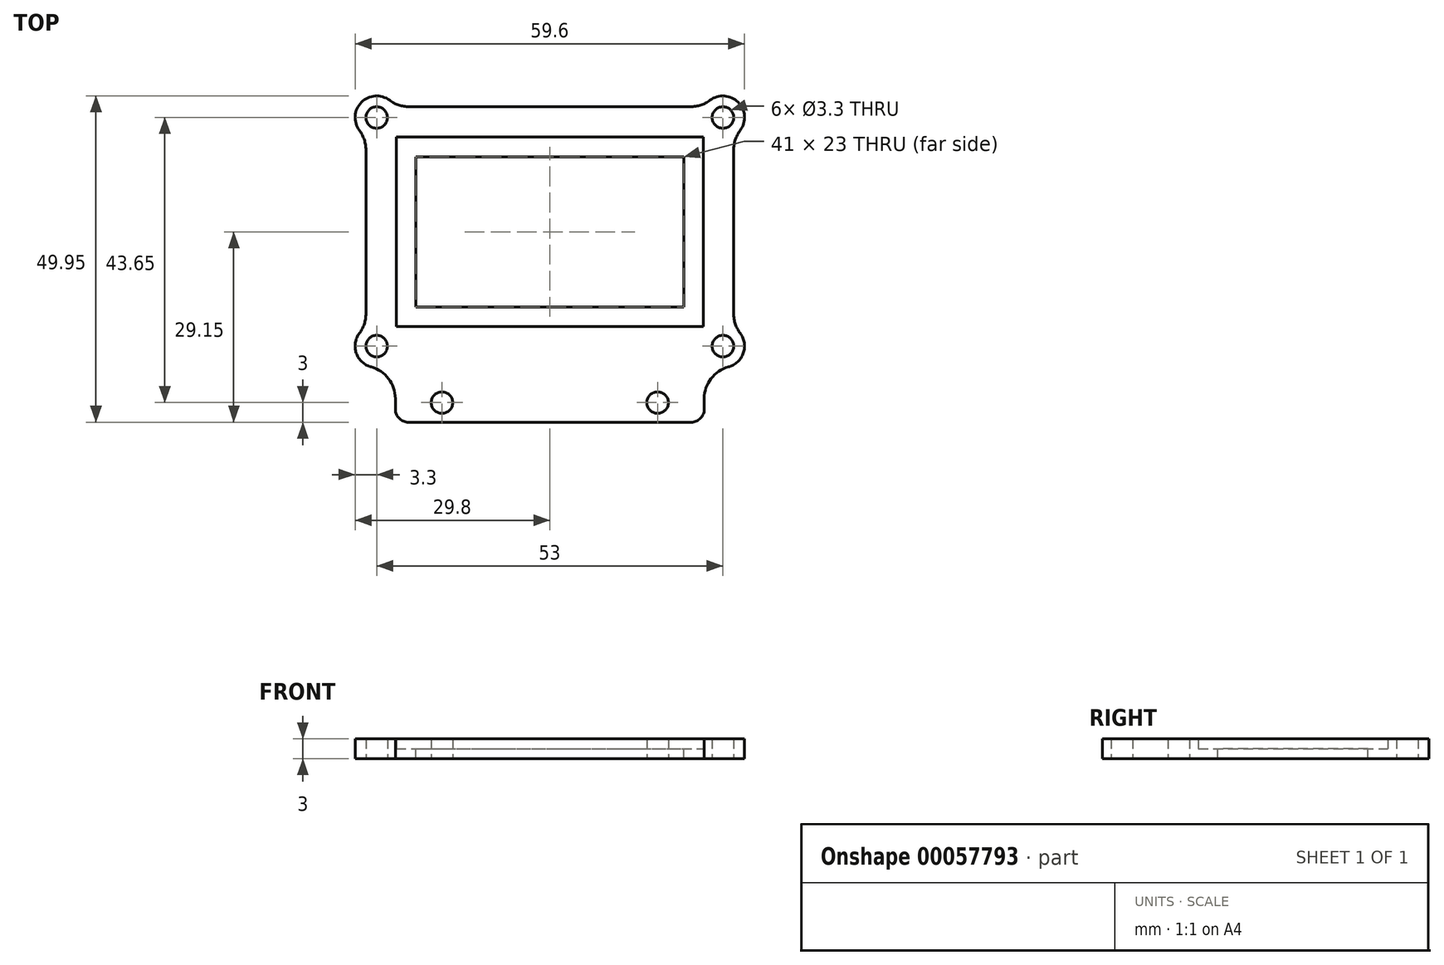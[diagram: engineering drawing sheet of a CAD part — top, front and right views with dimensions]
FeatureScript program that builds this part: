
annotation { "Feature Type Name" : "Feature", "Feature Type Description" : "" }
export const myFeature = defineFeature(function(context is Context, id is Id, definition is map)
    precondition{}
    {
        {
            var Q0;
            Q0=qCreatedBy(makeId("Top.planeOp"),FACE);
            var sketch = newSketch(context, id + "F0", { "sketchPlane" : qUnion([Q0])});
            skLineSegment(sketch, "E0", {"start": v(0, 0) * mm, "end": v(0, 49.8) * mm, "construction": true});
            skLineSegment(sketch, "E1.0", {"start": v(23.5, 0) * mm, "end": v(23.5, 29) * mm});
            skLineSegment(sketch, "E2.0", {"start": v(-23.5, 0) * mm, "end": v(-23.5, 29) * mm});
            skLineSegment(sketch, "E3", {"start": v(-23.5, 0) * mm, "end": v(23.5, 0) * mm});
            skLineSegment(sketch, "E4.0", {"start": v(-23.5, 29) * mm, "end": v(23.5, 29) * mm});
            skLineSegment(sketch, "E5.0", {"start": v(-26.5, 0) * mm, "end": v(-26.5, 33.65) * mm, "construction": true});
            skLineSegment(sketch, "E6.0", {"start": v(-26.5, 32) * mm, "end": v(30.75, 32) * mm, "construction": true});
            skLineSegment(sketch, "E7.0", {"start": v(26.5, 0) * mm, "end": v(26.5, 32) * mm, "construction": true});
            skLineSegment(sketch, "E8.0", {"start": v(-23.5, -3) * mm, "end": v(23.5, -3) * mm, "construction": true});
            skCircle(sketch, "E9", {"center": v(-26.5, 32) * mm, "radius": 1.65 * mm});
            skArc(sketch, "E10", {"start": v(-24.53, 34.64) * mm, "mid": v(-28.83, 34.33) * mm, "end": v(-29.14, 30.02) * mm});
            skArc(sketch, "E11.MirrorC", {"start": v(24.53, 34.64) * mm, "mid": v(28.83, 34.33) * mm, "end": v(29.14, 30.02) * mm});
            skCircle(sketch, "E12.MirrorC", {"center": v(26.5, 32) * mm, "radius": 1.65 * mm});
            skLineSegment(sketch, "E13", {"start": v(-21.53, 33.65) * mm, "end": v(21.53, 33.65) * mm});
            skLineSegment(sketch, "E14", {"start": v(-23.5, 14.5) * mm, "end": v(23.5, 14.5) * mm, "construction": true});
            skArc(sketch, "E15.MirrorC", {"start": v(-27.35, -6.19) * mm, "mid": v(-29.62, -4.08) * mm, "end": v(-29.14, -1.02) * mm});
            skCircle(sketch, "E16.MirrorC", {"center": v(-26.5, -3) * mm, "radius": 1.65 * mm});
            skArc(sketch, "E17.MirrorC", {"start": v(27.35, -6.19) * mm, "mid": v(29.62, -4.08) * mm, "end": v(29.14, -1.02) * mm});
            skCircle(sketch, "E18.MirrorC", {"center": v(26.5, -3) * mm, "radius": 1.65 * mm});
            skLineSegment(sketch, "E19", {"start": v(-28.15, 32.12) * mm, "end": v(-28.15, 31.88) * mm});
            skLineSegment(sketch, "E20.MirrorCS", {"start": v(28.15, 32.12) * mm, "end": v(28.15, 31.88) * mm});
            skLineSegment(sketch, "E21.trimOffspring", {"start": v(-28.15, 27.03) * mm, "end": v(-28.15, 1.97) * mm});
            skPoint(sketch, "E22.orphan", {"position": v(-28.15, -2.88) * mm});
            skPoint(sketch, "E23.orphan", {"position": v(28.15, -2.88) * mm});
            skLineSegment(sketch, "E24.trimOffspring", {"start": v(28.15, 27.03) * mm, "end": v(28.15, 1.97) * mm});
            skPoint(sketch, "E25.visualSharp", {"position": v(-28.15, 29.14) * mm});
            skArc(sketch, "E25.filletArc", {"start": v(-28.15, 27.03) * mm, "mid": v(-28.4, 28.6) * mm, "end": v(-29.14, 30.02) * mm});
            skPoint(sketch, "E26.visualSharp", {"position": v(-28.15, -0.14) * mm});
            skArc(sketch, "E26.filletArc", {"start": v(-29.14, -1.02) * mm, "mid": v(-28.4, 0.4) * mm, "end": v(-28.15, 1.97) * mm});
            skPoint(sketch, "E27.visualSharp", {"position": v(-23.64, 33.65) * mm});
            skArc(sketch, "E27.filletArc", {"start": v(-24.53, 34.64) * mm, "mid": v(-23.1, 33.9) * mm, "end": v(-21.53, 33.65) * mm});
            skPoint(sketch, "E28.visualSharp", {"position": v(23.64, 33.65) * mm});
            skArc(sketch, "E28.filletArc", {"start": v(21.53, 33.65) * mm, "mid": v(23.1, 33.9) * mm, "end": v(24.53, 34.64) * mm});
            skPoint(sketch, "E29.visualSharp", {"position": v(28.15, 29.14) * mm});
            skArc(sketch, "E29.filletArc", {"start": v(29.14, 30.02) * mm, "mid": v(28.4, 28.6) * mm, "end": v(28.15, 27.03) * mm});
            skPoint(sketch, "E30.visualSharp", {"position": v(28.15, -0.14) * mm});
            skArc(sketch, "E30.filletArc", {"start": v(28.15, 1.97) * mm, "mid": v(28.4, 0.4) * mm, "end": v(29.14, -1.02) * mm});
            skLineSegment(sketch, "E31", {"start": v(-23.64, -9.65) * mm, "end": v(-23.64, -9.65) * mm});
            skLineSegment(sketch, "E32", {"start": v(0, 0) * mm, "end": v(0, -14.65) * mm, "construction": true});
            skPoint(sketch, "E33.orphan", {"position": v(0, -6) * mm});
            skLineSegment(sketch, "E34.0", {"start": v(-16.5, 0) * mm, "end": v(-16.5, -14.65) * mm, "construction": true});
            skLineSegment(sketch, "E35.0", {"start": v(16.5, 0) * mm, "end": v(16.5, -14.65) * mm, "construction": true});
            skLineSegment(sketch, "E36.0", {"start": v(-23.64, -11.65) * mm, "end": v(23.64, -11.65) * mm, "construction": true});
            skCircle(sketch, "E37", {"center": v(-16.5, -11.65) * mm, "radius": 1.65 * mm});
            skCircle(sketch, "E38.MirrorC", {"center": v(16.5, -11.65) * mm, "radius": 1.65 * mm});
            skPoint(sketch, "E39.visualSharp", {"position": v(-23.64, -4.65) * mm});
            skArc(sketch, "E39.filletArc", {"start": v(-23.64, -11.02) * mm, "mid": v(-24.68, -7.97) * mm, "end": v(-27.35, -6.19) * mm});
            skPoint(sketch, "E40.visualSharp", {"position": v(-23.64, -14.65) * mm});
            skPoint(sketch, "E41.visualSharp", {"position": v(23.64, -4.65) * mm});
            skLineSegment(sketch, "E42", {"start": v(-21.64, -14.65) * mm, "end": v(21.64, -14.65) * mm});
            skLineSegment(sketch, "E43", {"start": v(23.64, -11.02) * mm, "end": v(23.64, -12.65) * mm});
            skArc(sketch, "E44.filletArc", {"start": v(27.35, -6.19) * mm, "mid": v(24.68, -7.97) * mm, "end": v(23.64, -11.02) * mm});
            skArc(sketch, "E45.filletArc", {"start": v(21.64, -14.65) * mm, "mid": v(23.06, -14.06) * mm, "end": v(23.64, -12.65) * mm});
            skLineSegment(sketch, "E46", {"start": v(-23.64, -11.02) * mm, "end": v(-23.64, -12.65) * mm});
            skArc(sketch, "E47.filletArc", {"start": v(-23.64, -12.65) * mm, "mid": v(-23.06, -14.06) * mm, "end": v(-21.64, -14.65) * mm});
            skSolve(sketch);
        }
        {
            var Q0;
            Q0=makeQuery(id+"F0.imprint","IMPRINT",FACE,{"disambiguationData":[TD([[makeQuery(id+"F0.imprint","IMPRINT",EDGE,{"derivedFrom":sQuery(id+"F0.wireOp",EDGE,"E1.0")}),1.0]])]});
            extrude(context, id + "F1", {"entities" : qUnion([Q0]), "depth" : 1.5 * mm});
        }
        {
            var Q0;
            Q0 = qSketchRegion(id + "F0", true);
            extrude(context, id + "F2", {"entities" : qUnion([Q0]), "operationType" : NewBodyOperationType.ADD, "depth" : 3 * mm});
        }
        {
            var Q0;
            Q0=makeQuery(id+"F1.opExtrude","CAP_FACE",FACE,{"disambiguationData":[OSD([sQuery(id+"F0.wireOp",EDGE,"E1.0"),sQuery(id+"F0.wireOp",EDGE,"E2.0"),sQuery(id+"F0.wireOp",EDGE,"E3"),sQuery(id+"F0.wireOp",EDGE,"E4.0")])],"isStart":false});
            var sketch = newSketch(context, id + "F3", { "sketchPlane" : qUnion([Q0])});
            skLineSegment(sketch, "E48.bottom", {"start": v(-23.5, 29) * mm, "end": v(23.5, 29) * mm, "construction": true});
            skLineSegment(sketch, "E48.top", {"start": v(-23.5, 0) * mm, "end": v(23.5, 0) * mm, "construction": true});
            skLineSegment(sketch, "E48.left", {"start": v(-23.5, 29) * mm, "end": v(-23.5, 0) * mm, "construction": true});
            skLineSegment(sketch, "E48.right", {"start": v(23.5, 29) * mm, "end": v(23.5, 0) * mm, "construction": true});
            skLineSegment(sketch, "E49.0", {"start": v(-20.5, 26) * mm, "end": v(20.5, 26) * mm});
            skLineSegment(sketch, "E50.0", {"start": v(-20.5, 26) * mm, "end": v(-20.5, 3) * mm});
            skLineSegment(sketch, "E51.0", {"start": v(-20.5, 3) * mm, "end": v(20.5, 3) * mm});
            skLineSegment(sketch, "E52.0", {"start": v(20.5, 26) * mm, "end": v(20.5, 3) * mm});
            skSolve(sketch);
        }
        {
            var Q0;
            Q0=makeQuery(id+"F3.imprint","IMPRINT",FACE,{"disambiguationData":[TD([[makeQuery(id+"F3.imprint","IMPRINT",EDGE,{"derivedFrom":sQuery(id+"F3.wireOp",EDGE,"E49.0")}),-1.0]])]});
            extrude(context, id + "F4", {"entities" : qUnion([Q0]), "operationType" : NewBodyOperationType.REMOVE, "oppositeDirection" : true, "depth" : 1.5 * mm, "hasSecondDirection" : true, "secondDirectionOppositeDirection" : false, "secondDirectionDepth" : 25 * mm});
        }
    });
